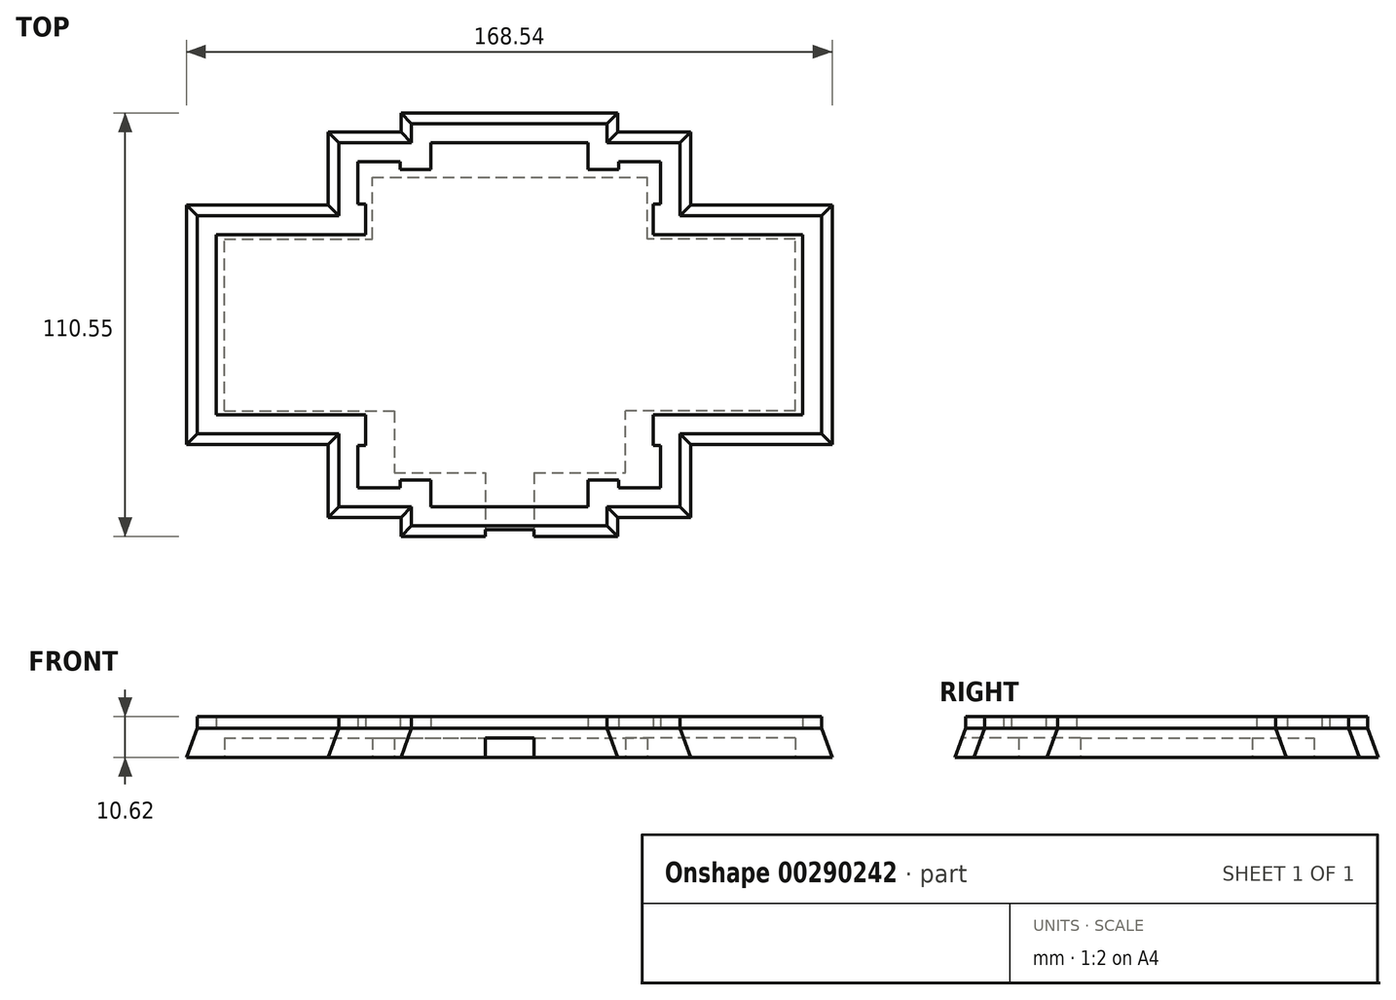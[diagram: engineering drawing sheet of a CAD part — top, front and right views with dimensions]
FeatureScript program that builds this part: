
annotation { "Feature Type Name" : "Feature", "Feature Type Description" : "" }
export const myFeature = defineFeature(function(context is Context, id is Id, definition is map)
    precondition{}
    {
        {
            var Q0;
            Q0=qCreatedBy(makeId("Top.planeOp"),FACE);
            var sketch = newSketch(context, id + "F0", { "sketchPlane" : qUnion([Q0])});
            skLineSegment(sketch, "E0", {"start": v(-69.2, 31.72) * mm, "end": v(-30.2, 31.72) * mm});
            skLineSegment(sketch, "E1", {"start": v(-30.2, 31.72) * mm, "end": v(-30.2, 39.72) * mm});
            skLineSegment(sketch, "E2", {"start": v(-30.2, 39.72) * mm, "end": v(-32.2, 39.72) * mm});
            skLineSegment(sketch, "E3", {"start": v(-32.2, 39.72) * mm, "end": v(-32.2, 50.72) * mm});
            skLineSegment(sketch, "E4", {"start": v(-32.2, 50.72) * mm, "end": v(-21.2, 50.72) * mm});
            skLineSegment(sketch, "E5", {"start": v(-21.2, 50.72) * mm, "end": v(-21.2, 48.72) * mm});
            skLineSegment(sketch, "E6", {"start": v(-21.2, 48.72) * mm, "end": v(-13.2, 48.72) * mm});
            skLineSegment(sketch, "E7", {"start": v(-13.2, 48.72) * mm, "end": v(-13.2, 55.72) * mm});
            skLineSegment(sketch, "E8", {"start": v(-13.2, 55.72) * mm, "end": v(7.3, 55.72) * mm});
            skLineSegment(sketch, "E9", {"start": v(-69.2, 31.72) * mm, "end": v(-69.2, 8.22) * mm});
            skLineSegment(sketch, "E10.MirrorCS", {"start": v(27.8, 55.72) * mm, "end": v(7.3, 55.72) * mm});
            skLineSegment(sketch, "E11.MirrorCS", {"start": v(27.8, 48.72) * mm, "end": v(27.8, 55.72) * mm});
            skLineSegment(sketch, "E12.MirrorCS", {"start": v(35.8, 48.72) * mm, "end": v(27.8, 48.72) * mm});
            skLineSegment(sketch, "E13.MirrorCS", {"start": v(35.8, 50.72) * mm, "end": v(35.8, 48.72) * mm});
            skLineSegment(sketch, "E14.MirrorCS", {"start": v(46.8, 50.72) * mm, "end": v(35.8, 50.72) * mm});
            skLineSegment(sketch, "E15.MirrorCS", {"start": v(46.8, 39.72) * mm, "end": v(46.8, 50.72) * mm});
            skLineSegment(sketch, "E16.MirrorCS", {"start": v(44.8, 39.72) * mm, "end": v(46.8, 39.72) * mm});
            skLineSegment(sketch, "E17.MirrorCS", {"start": v(44.8, 31.72) * mm, "end": v(44.8, 39.72) * mm});
            skLineSegment(sketch, "E18.MirrorCS", {"start": v(83.8, 31.72) * mm, "end": v(44.8, 31.72) * mm});
            skLineSegment(sketch, "E19.MirrorCS", {"start": v(83.8, 31.72) * mm, "end": v(83.8, 8.22) * mm});
            skLineSegment(sketch, "E20.MirrorCS", {"start": v(83.8, -15.28) * mm, "end": v(83.8, 8.22) * mm});
            skLineSegment(sketch, "E21.MirrorCS", {"start": v(83.8, -15.28) * mm, "end": v(44.8, -15.28) * mm});
            skLineSegment(sketch, "E22.MirrorCS", {"start": v(44.8, -15.28) * mm, "end": v(44.8, -23.28) * mm});
            skLineSegment(sketch, "E23.MirrorCS", {"start": v(44.8, -23.28) * mm, "end": v(46.8, -23.28) * mm});
            skLineSegment(sketch, "E24.MirrorCS", {"start": v(46.8, -23.28) * mm, "end": v(46.8, -34.28) * mm});
            skLineSegment(sketch, "E25.MirrorCS", {"start": v(46.8, -34.28) * mm, "end": v(35.8, -34.28) * mm});
            skLineSegment(sketch, "E26.MirrorCS", {"start": v(35.8, -34.28) * mm, "end": v(35.8, -32.28) * mm});
            skLineSegment(sketch, "E27.MirrorCS", {"start": v(35.8, -32.28) * mm, "end": v(27.8, -32.28) * mm});
            skLineSegment(sketch, "E28.MirrorCS", {"start": v(27.8, -32.28) * mm, "end": v(27.8, -39.28) * mm});
            skLineSegment(sketch, "E29.MirrorCS", {"start": v(27.8, -39.28) * mm, "end": v(7.3, -39.28) * mm});
            skLineSegment(sketch, "E30.MirrorCS", {"start": v(-13.2, -39.28) * mm, "end": v(7.3, -39.28) * mm});
            skLineSegment(sketch, "E31.MirrorCS", {"start": v(-13.2, -32.28) * mm, "end": v(-13.2, -39.28) * mm});
            skLineSegment(sketch, "E32.MirrorCS", {"start": v(-21.2, -32.28) * mm, "end": v(-13.2, -32.28) * mm});
            skLineSegment(sketch, "E33.MirrorCS", {"start": v(-21.2, -34.28) * mm, "end": v(-21.2, -32.28) * mm});
            skLineSegment(sketch, "E34.MirrorCS", {"start": v(-32.2, -34.28) * mm, "end": v(-21.2, -34.28) * mm});
            skLineSegment(sketch, "E35.MirrorCS", {"start": v(-32.2, -23.28) * mm, "end": v(-32.2, -34.28) * mm});
            skLineSegment(sketch, "E36.MirrorCS", {"start": v(-30.2, -23.28) * mm, "end": v(-32.2, -23.28) * mm});
            skLineSegment(sketch, "E37.MirrorCS", {"start": v(-30.2, -15.28) * mm, "end": v(-30.2, -23.28) * mm});
            skLineSegment(sketch, "E38.MirrorCS", {"start": v(-69.2, -15.28) * mm, "end": v(-30.2, -15.28) * mm});
            skLineSegment(sketch, "E39.MirrorCS", {"start": v(-69.2, -15.28) * mm, "end": v(-69.2, 8.22) * mm});
            skLineSegment(sketch, "E40.0", {"start": v(32.8, 55.72) * mm, "end": v(32.8, 60.72) * mm});
            skLineSegment(sketch, "E40.1", {"start": v(-37.2, -39.28) * mm, "end": v(-18.2, -39.28) * mm});
            skLineSegment(sketch, "E40.2", {"start": v(-37.2, -20.28) * mm, "end": v(-37.2, -39.28) * mm});
            skLineSegment(sketch, "E40.3", {"start": v(-74.2, -20.28) * mm, "end": v(-37.2, -20.28) * mm});
            skLineSegment(sketch, "E40.4", {"start": v(-74.2, -20.28) * mm, "end": v(-74.2, 8.22) * mm});
            skLineSegment(sketch, "E40.5", {"start": v(-74.2, 36.72) * mm, "end": v(-74.2, 8.22) * mm});
            skLineSegment(sketch, "E40.6", {"start": v(-74.2, 36.72) * mm, "end": v(-37.2, 36.72) * mm});
            skLineSegment(sketch, "E40.7", {"start": v(-18.2, 60.72) * mm, "end": v(7.3, 60.72) * mm});
            skLineSegment(sketch, "E40.8", {"start": v(-18.2, 55.72) * mm, "end": v(-18.2, 60.72) * mm});
            skLineSegment(sketch, "E40.9", {"start": v(-37.2, 55.72) * mm, "end": v(-18.2, 55.72) * mm});
            skLineSegment(sketch, "E40.10", {"start": v(-37.2, 36.72) * mm, "end": v(-37.2, 55.72) * mm});
            skLineSegment(sketch, "E40.11", {"start": v(-18.2, -39.28) * mm, "end": v(-18.2, -44.28) * mm});
            skLineSegment(sketch, "E40.12", {"start": v(32.8, 60.72) * mm, "end": v(7.3, 60.72) * mm});
            skLineSegment(sketch, "E40.13", {"start": v(-18.2, -44.28) * mm, "end": v(7.3, -44.28) * mm});
            skLineSegment(sketch, "E40.14", {"start": v(32.8, -44.28) * mm, "end": v(7.3, -44.28) * mm});
            skLineSegment(sketch, "E40.15", {"start": v(32.8, -39.28) * mm, "end": v(32.8, -44.28) * mm});
            skLineSegment(sketch, "E40.16", {"start": v(51.8, -39.28) * mm, "end": v(32.8, -39.28) * mm});
            skLineSegment(sketch, "E40.17", {"start": v(51.8, -20.28) * mm, "end": v(51.8, -39.28) * mm});
            skLineSegment(sketch, "E40.18", {"start": v(88.8, -20.28) * mm, "end": v(51.8, -20.28) * mm});
            skLineSegment(sketch, "E40.19", {"start": v(88.8, -20.28) * mm, "end": v(88.8, 8.22) * mm});
            skLineSegment(sketch, "E40.20", {"start": v(88.8, 36.72) * mm, "end": v(88.8, 8.22) * mm});
            skLineSegment(sketch, "E40.21", {"start": v(88.8, 36.72) * mm, "end": v(51.8, 36.72) * mm});
            skLineSegment(sketch, "E40.22", {"start": v(51.8, 36.72) * mm, "end": v(51.8, 55.72) * mm});
            skLineSegment(sketch, "E40.23", {"start": v(51.8, 55.72) * mm, "end": v(32.8, 55.72) * mm});
            skSolve(sketch);
        }
        {
            var Q0;
            Q0=makeQuery(id+"F0.imprint","IMPRINT",FACE,{"disambiguationData":[TD([[makeQuery(id+"F0.imprint","IMPRINT",EDGE,{"derivedFrom":sQuery(id+"F0.wireOp",EDGE,"E0")}),1.0]])]});
            extrude(context, id + "F1", {"entities" : qUnion([Q0]), "depth" : 3 * mm});
        }
        {
            var Q0;
            Q0=makeQuery(id+"F0.imprint","IMPRINT",FACE,{"disambiguationData":[TD([[makeQuery(id+"F0.imprint","IMPRINT",EDGE,{"derivedFrom":sQuery(id+"F0.wireOp",EDGE,"E0")}),-1.0]])]});
            var Q1;
            Q1=makeQuery(id+"F0.imprint","IMPRINT",FACE,{"disambiguationData":[TD([[makeQuery(id+"F0.imprint","IMPRINT",EDGE,{"derivedFrom":sQuery(id+"F0.wireOp",EDGE,"E0")}),1.0]])]});
            extrude(context, id + "F2", {"entities" : qUnion([Q0, Q1]), "operationType" : NewBodyOperationType.ADD, "oppositeDirection" : true, "depth" : 7.62 * mm, "hasDraft" : true, "draftAngle" : 20 * degree});
        }
        {
            var Q0;
            Q0=makeQuery(id+"F2.opExtrude","CAP_FACE",FACE,{"disambiguationData":[OSD([sQuery(id+"F0.wireOp",EDGE,"E40.0"),sQuery(id+"F0.wireOp",EDGE,"E40.1"),sQuery(id+"F0.wireOp",EDGE,"E40.2"),sQuery(id+"F0.wireOp",EDGE,"E40.3"),sQuery(id+"F0.wireOp",EDGE,"E40.4"),sQuery(id+"F0.wireOp",EDGE,"E40.5"),sQuery(id+"F0.wireOp",EDGE,"E40.6"),sQuery(id+"F0.wireOp",EDGE,"E40.7"),sQuery(id+"F0.wireOp",EDGE,"E40.8"),sQuery(id+"F0.wireOp",EDGE,"E40.9"),sQuery(id+"F0.wireOp",EDGE,"E40.10"),sQuery(id+"F0.wireOp",EDGE,"E40.11"),sQuery(id+"F0.wireOp",EDGE,"E40.12"),sQuery(id+"F0.wireOp",EDGE,"E40.13"),sQuery(id+"F0.wireOp",EDGE,"E40.14"),sQuery(id+"F0.wireOp",EDGE,"E40.15"),sQuery(id+"F0.wireOp",EDGE,"E40.16"),sQuery(id+"F0.wireOp",EDGE,"E40.17"),sQuery(id+"F0.wireOp",EDGE,"E40.18"),sQuery(id+"F0.wireOp",EDGE,"E40.19"),sQuery(id+"F0.wireOp",EDGE,"E40.20"),sQuery(id+"F0.wireOp",EDGE,"E40.21"),sQuery(id+"F0.wireOp",EDGE,"E40.22"),sQuery(id+"F0.wireOp",EDGE,"E40.23")])],"isStart":false});
            var sketch = newSketch(context, id + "F3", { "sketchPlane" : qUnion([Q0])});
            skLineSegment(sketch, "E41", {"start": v(-67.1, 14.3) * mm, "end": v(-67.1, -30.62) * mm});
            skLineSegment(sketch, "E42", {"start": v(-67.1, -30.62) * mm, "end": v(-28.47, -30.62) * mm});
            skLineSegment(sketch, "E43", {"start": v(-28.47, -30.62) * mm, "end": v(-28.47, -46.67) * mm});
            skLineSegment(sketch, "E44", {"start": v(-67.1, 14.3) * mm, "end": v(-28.47, 14.3) * mm});
            skLineSegment(sketch, "E45.MirrorCS", {"start": v(-22.76, 14.3) * mm, "end": v(-22.76, 30.35) * mm});
            skLineSegment(sketch, "E46", {"start": v(-22.76, 30.35) * mm, "end": v(1.09, 30.35) * mm});
            skLineSegment(sketch, "E47", {"start": v(37.64, 30.35) * mm, "end": v(37.64, 14.3) * mm});
            skLineSegment(sketch, "E48.MirrorCS", {"start": v(81.97, 14.3) * mm, "end": v(43.35, 14.3) * mm});
            skLineSegment(sketch, "E49.MirrorCS", {"start": v(81.97, 14.3) * mm, "end": v(81.97, -30.62) * mm});
            skLineSegment(sketch, "E50.MirrorCS", {"start": v(81.97, -30.62) * mm, "end": v(43.35, -30.62) * mm});
            skLineSegment(sketch, "E51.MirrorCS", {"start": v(43.35, -30.62) * mm, "end": v(43.35, -46.67) * mm});
            skLineSegment(sketch, "E52", {"start": v(-28.47, -46.67) * mm, "end": v(43.35, -46.67) * mm});
            skPoint(sketch, "E53.start.orphan", {"position": v(7.44, 30.35) * mm});
            skPoint(sketch, "E54.start.orphan", {"position": v(-67.1, -8.16) * mm});
            skLineSegment(sketch, "E55", {"start": v(1.09, 30.35) * mm, "end": v(1.09, 47.06) * mm});
            skLineSegment(sketch, "E56", {"start": v(13.79, 30.35) * mm, "end": v(13.79, 47.06) * mm});
            skLineSegment(sketch, "E57", {"start": v(-28.47, 14.3) * mm, "end": v(-22.76, 14.3) * mm});
            skLineSegment(sketch, "E58", {"start": v(43.35, 14.3) * mm, "end": v(37.64, 14.3) * mm});
            skLineSegment(sketch, "E59.trimOffspring", {"start": v(13.79, 30.35) * mm, "end": v(37.64, 30.35) * mm});
            skLineSegment(sketch, "E60", {"start": v(1.09, 47.06) * mm, "end": v(13.79, 47.06) * mm});
            skSolve(sketch);
        }
        {
            var Q0;
            Q0 = qSketchRegion(id + "F3", true);
            extrude(context, id + "F4", {"entities" : qUnion([Q0]), "operationType" : NewBodyOperationType.REMOVE, "oppositeDirection" : true, "depth" : 5.08 * mm});
        }
    });
